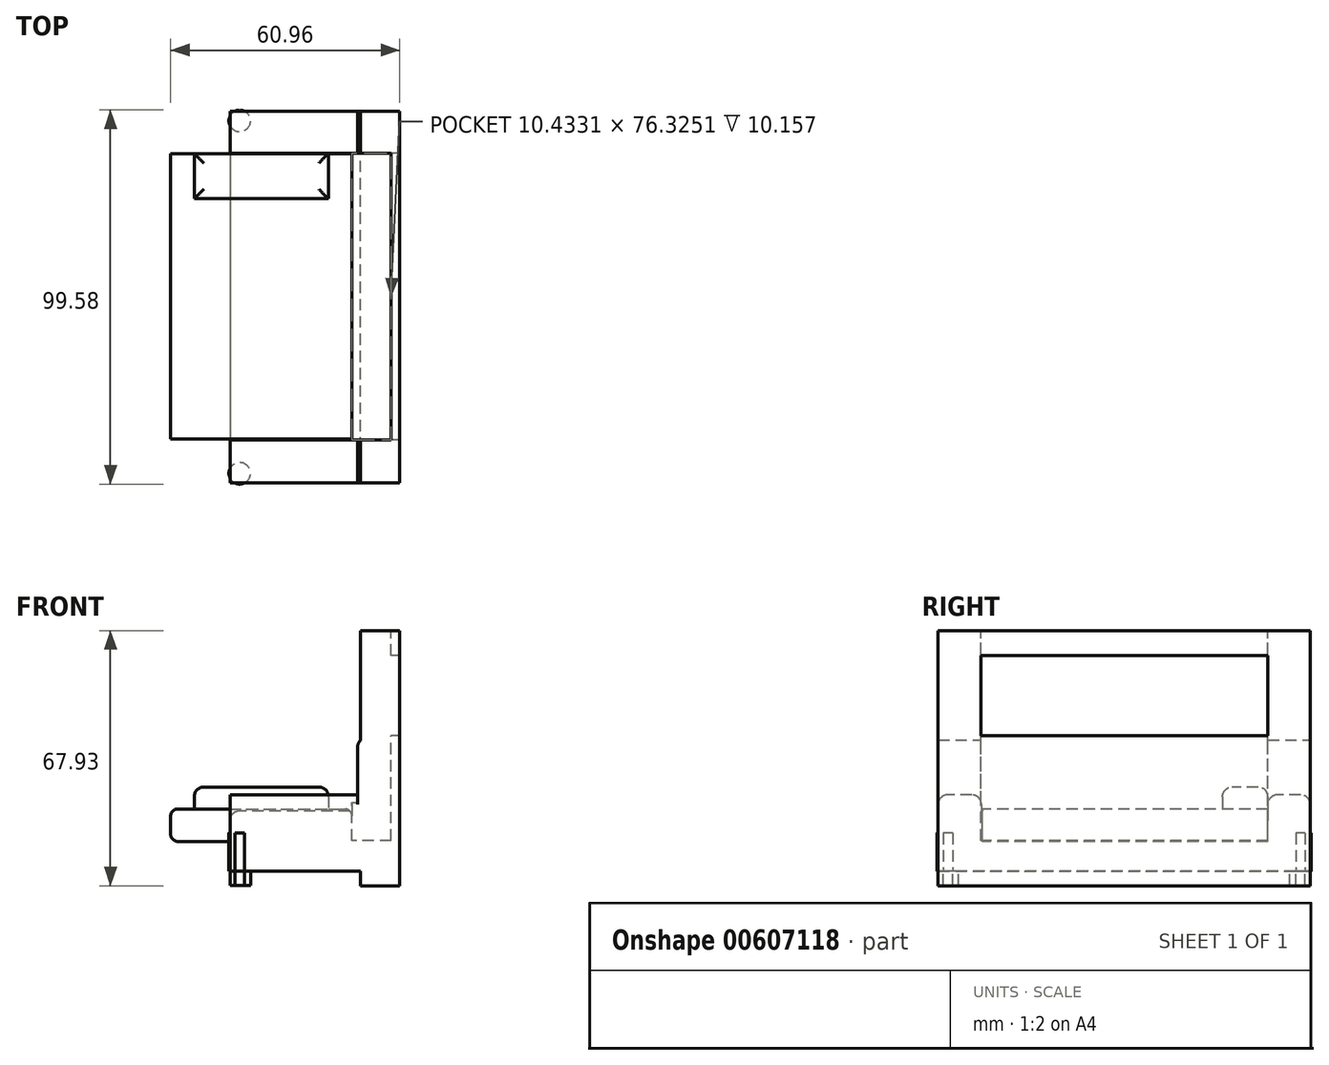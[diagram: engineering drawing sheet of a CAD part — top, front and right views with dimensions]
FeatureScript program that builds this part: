
annotation { "Feature Type Name" : "Feature", "Feature Type Description" : "" }
export const myFeature = defineFeature(function(context is Context, id is Id, definition is map)
    precondition{}
    {
        {
            var Q0;
            Q0=qCreatedBy(makeId("Top.planeOp"),FACE);
            var sketch = newSketch(context, id + "F0", { "sketchPlane" : qUnion([Q0])});
            skLineSegment(sketch, "E0.bottom", {"start": v(-36.7, 51.66) * mm, "end": v(8.5, 51.66) * mm});
            skLineSegment(sketch, "E0.top", {"start": v(-36.7, -47.34) * mm, "end": v(8.5, -47.34) * mm});
            skLineSegment(sketch, "E0.left", {"start": v(-36.7, 51.66) * mm, "end": v(-36.7, -47.34) * mm});
            skLineSegment(sketch, "E0.right", {"start": v(8.5, 51.66) * mm, "end": v(8.5, -47.34) * mm});
            skCircle(sketch, "E1", {"center": v(-34.1, 49.07) * mm, "radius": 2.88 * mm});
            skLineSegment(sketch, "E2", {"start": v(-14.1, 58) * mm, "end": v(-14.1, -55.7) * mm});
            skPoint(sketch, "E2.startSnap0", {"position": v(-14.1, 51.66) * mm});
            skLineSegment(sketch, "E3", {"start": v(-36.7, 2.16) * mm, "end": v(19.43, 2.16) * mm});
            skCircle(sketch, "E4.MirrorC", {"center": v(-34.1, -44.75) * mm, "radius": 2.88 * mm});
            skSolve(sketch);
        }
        {
            var Q0;
            Q0=qSketchRegion(id+"F0",true);
            extrude(context, id + "F1", {"entities" : qUnion([Q0]), "depth" : 10.16 * mm, "offsetDistance" : 25.4 * mm});
        }
        {
            var Q0;
            {var subQ0=sQuery(id+"F0.wireOp",EDGE,"51a0da69-c7e2-46c1-813b-57cbcf78bc440.MirrorC");var subQ1=sQuery(id+"F0.wireOp",EDGE,"E0.bottom");var subQ2=makeQuery(id+"F0.imprint","INTERSECT",VERTEX,{"disambiguationData":[OD(0.0)],"derivedFrom":[subQ1,subQ0]});Q0=makeQuery(id+"F0.imprint","IMPRINT",FACE,{"disambiguationData":[TD([[makeQuery(id+"F0.imprint","IMPRINT",EDGE,{"disambiguationData":[TD([[subQ2,-1.0]])],"derivedFrom":subQ1}),-1.0]])]});}
            var Q1;
            {var subQ0=sQuery(id+"F0.wireOp",EDGE,"E1");var subQ1=sQuery(id+"F0.wireOp",EDGE,"E0.bottom");var subQ2=makeQuery(id+"F0.imprint","INTERSECT",VERTEX,{"disambiguationData":[OD(0.0)],"derivedFrom":[subQ1,subQ0]});Q1=makeQuery(id+"F0.imprint","IMPRINT",FACE,{"disambiguationData":[TD([[makeQuery(id+"F0.imprint","IMPRINT",EDGE,{"disambiguationData":[TD([[subQ2,-1.0]])],"derivedFrom":subQ1}),-1.0]])]});}
            var Q2;
            {var subQ0=sQuery(id+"F0.wireOp",EDGE,"3a2c508c-d446-42d2-86cc-67812b7293b00.MirrorC");var subQ1=sQuery(id+"F0.wireOp",EDGE,"E0.top");var subQ2=makeQuery(id+"F0.imprint","INTERSECT",VERTEX,{"disambiguationData":[OD(0.0)],"derivedFrom":[subQ1,subQ0]});Q2=makeQuery(id+"F0.imprint","IMPRINT",FACE,{"disambiguationData":[TD([[makeQuery(id+"F0.imprint","IMPRINT",EDGE,{"disambiguationData":[TD([[subQ2,-1.0]])],"derivedFrom":subQ1}),1.0]])]});}
            var Q3;
            {var subQ0=sQuery(id+"F0.wireOp",EDGE,"E4.MirrorC");var subQ1=sQuery(id+"F0.wireOp",EDGE,"E0.top");var subQ2=makeQuery(id+"F0.imprint","INTERSECT",VERTEX,{"disambiguationData":[OD(0.0)],"derivedFrom":[subQ1,subQ0]});Q3=makeQuery(id+"F0.imprint","IMPRINT",FACE,{"disambiguationData":[TD([[makeQuery(id+"F0.imprint","IMPRINT",EDGE,{"disambiguationData":[TD([[subQ2,-1.0]])],"derivedFrom":subQ1}),1.0]])]});}
            extrude(context, id + "F2", {"entities" : qUnion([Q0, Q1, Q2, Q3]), "operationType" : NewBodyOperationType.ADD, "oppositeDirection" : true, "depth" : 3.8 * mm, "offsetDistance" : 25.4 * mm});
        }
        {
            var Q0;
            Q0=makeQuery(id+"F1.opExtrude","CAP_FACE",FACE,{"disambiguationData":[OSD([sQuery(id+"F0.wireOp",EDGE,"E0.bottom"),sQuery(id+"F0.wireOp",EDGE,"E0.top"),sQuery(id+"F0.wireOp",EDGE,"E0.left"),sQuery(id+"F0.wireOp",EDGE,"E0.right"),sQuery(id+"F0.wireOp",EDGE,"E1"),sQuery(id+"F0.wireOp",EDGE,"51a0da69-c7e2-46c1-813b-57cbcf78bc440.MirrorC"),sQuery(id+"F0.wireOp",EDGE,"E4.MirrorC"),sQuery(id+"F0.wireOp",EDGE,"3a2c508c-d446-42d2-86cc-67812b7293b00.MirrorC")])],"isStart":false});
            var sketch = newSketch(context, id + "F3", { "sketchPlane" : qUnion([Q0])});
            skLineSegment(sketch, "E5.bottom", {"start": v(8.5, 51.66) * mm, "end": v(-2.73, 51.66) * mm});
            skLineSegment(sketch, "E5.top", {"start": v(8.5, -47.34) * mm, "end": v(-2.73, -47.34) * mm});
            skLineSegment(sketch, "E5.left", {"start": v(8.5, 51.66) * mm, "end": v(8.5, -47.34) * mm});
            skLineSegment(sketch, "E5.right", {"start": v(-2.73, 51.66) * mm, "end": v(-2.73, -47.34) * mm});
            skSolve(sketch);
        }
        {
            var Q0;
            Q0=qSketchRegion(id+"F3",true);
            extrude(context, id + "F4", {"entities" : qUnion([Q0]), "operationType" : NewBodyOperationType.ADD, "depth" : 25.4 * mm, "offsetDistance" : 25.4 * mm});
        }
        {
            var Q0;
            {var subQ0=sQuery(id+"F0.wireOp",EDGE,"E0.left");var subQ1=sQuery(id+"F0.wireOp",EDGE,"E0.top");var subQ3=sQuery(id+"F0.wireOp",EDGE,"E4.MirrorC");var subQ7=sQuery(id+"F0.wireOp",EDGE,"E1");var subQ9=sQuery(id+"F0.wireOp",EDGE,"E0.bottom");var subQ12=sQuery(id+"F0.wireOp",EDGE,"E0.right");var subQ13=sQuery(id+"F0.wireOp",EDGE,"3a2c508c-d446-42d2-86cc-67812b7293b00.MirrorC");var subQ21=sQuery(id+"F0.wireOp",EDGE,"51a0da69-c7e2-46c1-813b-57cbcf78bc440.MirrorC");Q0=makeQuery(id+"F4.boolean.opBoolean","SPLIT",FACE,{"disambiguationData":[TD([makeQuery(id+"F4.opExtrude","SWEPT_FACE",FACE,{"disambiguationData":[OSD([sQuery(id+"F3.wireOp",EDGE,"E5.right")])]})])],"derivedFrom":makeQuery(id+"F1.opExtrude","CAP_FACE",FACE,{"disambiguationData":[OSD([subQ9,subQ1,subQ0,subQ12,subQ7,subQ21,subQ3,subQ13])],"isStart":false})});}
            var sketch = newSketch(context, id + "F5", { "sketchPlane" : qUnion([Q0])});
            skLineSegment(sketch, "E6.bottom", {"start": v(-2.73, 51.66) * mm, "end": v(-36.7, 51.66) * mm});
            skLineSegment(sketch, "E6.top", {"start": v(-2.73, 40.44) * mm, "end": v(-36.7, 40.44) * mm});
            skLineSegment(sketch, "E6.left", {"start": v(-2.73, 51.66) * mm, "end": v(-2.73, 40.44) * mm});
            skLineSegment(sketch, "E6.right", {"start": v(-36.7, 51.66) * mm, "end": v(-36.7, 40.44) * mm});
            skLineSegment(sketch, "E7.bottom", {"start": v(-2.73, -47.34) * mm, "end": v(-36.7, -47.34) * mm});
            skLineSegment(sketch, "E7.top", {"start": v(-2.73, -35.83) * mm, "end": v(-36.7, -35.83) * mm});
            skLineSegment(sketch, "E7.left", {"start": v(-2.73, -47.34) * mm, "end": v(-2.73, -35.83) * mm});
            skLineSegment(sketch, "E7.right", {"start": v(-36.7, -47.34) * mm, "end": v(-36.7, -35.83) * mm});
            skSolve(sketch);
        }
        {
            var Q0;
            {var subQ0=sQuery(id+"F5.wireOp",EDGE,"E6.top");Q0=makeQuery(id+"F5.imprint","IMPRINT",FACE,{"disambiguationData":[TD([[makeQuery(id+"F5.imprint","IMPRINT",EDGE,{"derivedFrom":subQ0}),-1.0]])]});}
            var Q1;
            {var subQ0=sQuery(id+"F5.wireOp",EDGE,"E7.top");Q1=makeQuery(id+"F5.imprint","IMPRINT",FACE,{"disambiguationData":[TD([[makeQuery(id+"F5.imprint","IMPRINT",EDGE,{"derivedFrom":subQ0}),1.0]])]});}
            extrude(context, id + "F6", {"entities" : qUnion([Q0, Q1]), "operationType" : NewBodyOperationType.ADD, "depth" : 10.16 * mm, "offsetDistance" : 25.4 * mm});
        }
        {
            var Q0;
            Q0=makeQuery(id+"F4.opExtrude","CAP_EDGE",EDGE,{"disambiguationData":[OSD([sQuery(id+"F3.wireOp",EDGE,"E5.right")])],"isStart":false});
            var Q1;
            Q1=makeQuery(id+"F6.opExtrude","CAP_EDGE",EDGE,{"disambiguationData":[OSD([sQuery(id+"F5.wireOp",EDGE,"E7.top")])],"isStart":false});
            var Q2;
            Q2=makeQuery(id+"F6.opExtrude","CAP_EDGE",EDGE,{"disambiguationData":[OSD([sQuery(id+"F5.wireOp",EDGE,"E7.bottom")])],"isStart":false});
            var Q3;
            Q3=makeQuery(id+"F6.opExtrude","CAP_EDGE",EDGE,{"disambiguationData":[OSD([sQuery(id+"F5.wireOp",EDGE,"E6.bottom")])],"isStart":false});
            var Q4;
            Q4=makeQuery(id+"F6.opExtrude","CAP_EDGE",EDGE,{"disambiguationData":[OSD([sQuery(id+"F5.wireOp",EDGE,"E6.top")])],"isStart":false});
            var Q5;
            Q5=makeQuery(id+"F4.opExtrude","CAP_EDGE",EDGE,{"disambiguationData":[OSD([sQuery(id+"F3.wireOp",EDGE,"E5.left")])],"isStart":false});
            fillet(context, id + "F7", {"entities" : qUnion([Q0, Q1, Q2, Q3, Q4, Q5]), "radius" : 2.54 * mm, "tangentPropagation" : true, "allowEdgeOverflow" : false});
        }
        {
            var Q0;
            {var subQ0=makeQuery(id+"F4.opExtrude","SWEPT_FACE",FACE,{"disambiguationData":[OSD([sQuery(id+"F3.wireOp",EDGE,"E5.right")])]});var subQ1=sQuery(id+"F0.wireOp",EDGE,"E0.left");var subQ2=sQuery(id+"F0.wireOp",EDGE,"E0.top");var subQ4=sQuery(id+"F0.wireOp",EDGE,"E4.MirrorC");var subQ9=sQuery(id+"F0.wireOp",EDGE,"E1");var subQ12=sQuery(id+"F0.wireOp",EDGE,"E0.bottom");var subQ16=sQuery(id+"F0.wireOp",EDGE,"E0.right");var subQ17=sQuery(id+"F0.wireOp",EDGE,"3a2c508c-d446-42d2-86cc-67812b7293b00.MirrorC");var subQ25=sQuery(id+"F0.wireOp",EDGE,"51a0da69-c7e2-46c1-813b-57cbcf78bc440.MirrorC");Q0=makeQuery(id+"F6.boolean.opBoolean","SPLIT",FACE,{"disambiguationData":[TD([subQ0])],"derivedFrom":makeQuery(id+"F4.boolean.opBoolean","SPLIT",FACE,{"disambiguationData":[TD([subQ0])],"derivedFrom":makeQuery(id+"F1.opExtrude","CAP_FACE",FACE,{"disambiguationData":[OSD([subQ12,subQ2,subQ1,subQ16,subQ9,subQ25,subQ4,subQ17])],"isStart":false})})});}
            var sketch = newSketch(context, id + "F8", { "sketchPlane" : qUnion([Q0])});
            skLineSegment(sketch, "E8.bottom", {"start": v(-2.73, 40.44) * mm, "end": v(-36.7, 40.44) * mm});
            skLineSegment(sketch, "E8.top", {"start": v(-2.73, 2.3) * mm, "end": v(-36.7, 2.3) * mm});
            skLineSegment(sketch, "E8.left", {"start": v(-2.73, 40.44) * mm, "end": v(-2.73, 2.3) * mm});
            skLineSegment(sketch, "E8.right", {"start": v(-36.7, 40.44) * mm, "end": v(-36.7, 2.3) * mm});
            skLineSegment(sketch, "E9.bottom", {"start": v(-2.73, -35.83) * mm, "end": v(-36.7, -35.83) * mm});
            skLineSegment(sketch, "E9.top", {"start": v(-2.73, 1.3) * mm, "end": v(-36.7, 1.3) * mm});
            skLineSegment(sketch, "E9.left", {"start": v(-2.73, -35.83) * mm, "end": v(-2.73, 1.3) * mm});
            skLineSegment(sketch, "E9.right", {"start": v(-36.7, -35.83) * mm, "end": v(-36.7, 1.3) * mm});
            skSolve(sketch);
        }
        {
            var Q0;
            Q0=makeQuery(id+"F8.imprint","IMPRINT",FACE,{"disambiguationData":[TD([[makeQuery(id+"F8.imprint","IMPRINT",EDGE,{"derivedFrom":sQuery(id+"F8.wireOp",EDGE,"E8.bottom")}),1.0]])]});
            var Q1;
            Q1=makeQuery(id+"F8.imprint","IMPRINT",FACE,{"disambiguationData":[TD([[makeQuery(id+"F8.imprint","IMPRINT",EDGE,{"derivedFrom":sQuery(id+"F8.wireOp",EDGE,"E9.bottom")}),-1.0]])]});
            extrude(context, id + "F9", {"entities" : qUnion([Q0, Q1]), "operationType" : NewBodyOperationType.ADD, "depth" : 5.84 * mm, "offsetDistance" : 25.4 * mm});
        }
        {
            var Q0;
            Q0=makeQuery(id+"F9.opExtrude","CAP_EDGE",EDGE,{"disambiguationData":[OSD([sQuery(id+"F8.wireOp",EDGE,"E9.top")])],"isStart":false});
            var Q1;
            Q1=makeQuery(id+"F9.opExtrude","CAP_EDGE",EDGE,{"disambiguationData":[OSD([sQuery(id+"F8.wireOp",EDGE,"E8.top")])],"isStart":false});
            var Q2;
            Q2=makeQuery(id+"F9.opExtrude","CAP_EDGE",EDGE,{"disambiguationData":[OSD([sQuery(id+"F8.wireOp",EDGE,"E9.right")])],"isStart":false});
            var Q3;
            Q3=makeQuery(id+"F9.opExtrude","CAP_EDGE",EDGE,{"disambiguationData":[OSD([sQuery(id+"F8.wireOp",EDGE,"E8.right")])],"isStart":false});
            fillet(context, id + "F10", {"entities" : qUnion([Q0, Q1, Q2, Q3]), "radius" : 2.54 * mm, "tangentPropagation" : true, "allowEdgeOverflow" : false});
        }
        {
            var Q0;
            {var subQ0=sQuery(id+"F0.wireOp",EDGE,"E0.right");var subQ2=makeQuery(id+"F0.imprint","INTERSECT",VERTEX,{"derivedFrom":[subQ0,sQuery(id+"F0.wireOp",EDGE,"E3")]});Q0=makeQuery(id+"F4.boolean.opBoolean","MERGE",FACE,{"derivedFrom":[makeQuery(id+"F1.opExtrude","SWEPT_FACE",FACE,{"disambiguationData":[OSD([subQ0]),TDD([makeQuery(id+"F0.imprint","IMPRINT",EDGE,{"disambiguationData":[TD([[makeQuery(id+"F0.imprint","INTERSECT",VERTEX,{"derivedFrom":[sQuery(id+"F0.wireOp",EDGE,"E0.bottom"),subQ0]}),-1.0]])],"derivedFrom":subQ0})])]}),makeQuery(id+"F1.opExtrude","SWEPT_FACE",FACE,{"disambiguationData":[OSD([subQ0]),TDD([makeQuery(id+"F0.imprint","IMPRINT",EDGE,{"disambiguationData":[TD([[subQ2,1.0]])],"derivedFrom":subQ0}),makeQuery(id+"F0.imprint","IMPRINT",EDGE,{"disambiguationData":[TD([[subQ2,-1.0]])],"derivedFrom":subQ0})])]}),makeQuery(id+"F1.opExtrude","SWEPT_FACE",FACE,{"disambiguationData":[OSD([subQ0]),TDD([makeQuery(id+"F0.imprint","IMPRINT",EDGE,{"disambiguationData":[TD([[makeQuery(id+"F0.imprint","INTERSECT",VERTEX,{"derivedFrom":[sQuery(id+"F0.wireOp",EDGE,"E0.top"),subQ0]}),1.0]])],"derivedFrom":subQ0})])]}),makeQuery(id+"F4.opExtrude","SWEPT_FACE",FACE,{"disambiguationData":[OSD([sQuery(id+"F3.wireOp",EDGE,"E5.left")])]})]});}
            var sketch = newSketch(context, id + "F11", { "sketchPlane" : qUnion([Q0])});
            skLineSegment(sketch, "E10.bottom", {"start": v(-47.34, 64.04) * mm, "end": v(51.66, 64.04) * mm});
            skLineSegment(sketch, "E10.top", {"start": v(-47.34, -3.89) * mm, "end": v(51.66, -3.89) * mm});
            skLineSegment(sketch, "E10.left", {"start": v(-47.34, 64.04) * mm, "end": v(-47.34, -3.89) * mm});
            skLineSegment(sketch, "E10.right", {"start": v(51.66, 64.04) * mm, "end": v(51.66, -3.89) * mm});
            skLineSegment(sketch, "E11.bottom", {"start": v(40.38, 7.91) * mm, "end": v(-35.6, 7.91) * mm});
            skLineSegment(sketch, "E11.top", {"start": v(40.38, 16.55) * mm, "end": v(-35.6, 16.55) * mm});
            skLineSegment(sketch, "E11.left", {"start": v(40.38, 7.91) * mm, "end": v(40.38, 16.55) * mm});
            skLineSegment(sketch, "E11.right", {"start": v(-35.6, 7.91) * mm, "end": v(-35.6, 16.55) * mm});
            skSolve(sketch);
        }
        {
            var Q0;
            Q0=qSketchRegion(id+"F11",true);
            extrude(context, id + "F12", {"entities" : qUnion([Q0]), "operationType" : NewBodyOperationType.ADD, "oppositeDirection" : true, "depth" : 10.4 * mm, "offsetDistance" : 25.4 * mm});
        }
        {
            var Q0;
            {var subQ0=sQuery(id+"F11.wireOp",EDGE,"E10.bottom");var subQ10=sQuery(id+"F11.wireOp",EDGE,"E10.left");var subQ11=sQuery(id+"F11.wireOp",EDGE,"E10.right");Q0=makeQuery(id+"F12.boolean.opBoolean","SPLIT",FACE,{"disambiguationData":[TD([makeQuery(id+"F7.opFillet","BLEND_FACE",FACE,{"disambiguationData":[OSD([sQuery(id+"F3.wireOp",EDGE,"E5.right")])]})])],"derivedFrom":makeQuery(id+"F12.opExtrude","CAP_FACE",FACE,{"disambiguationData":[OSD([subQ0,sQuery(id+"F11.wireOp",EDGE,"E10.top"),subQ10,subQ11])],"isStart":false})});}
            var sketch = newSketch(context, id + "F13", { "sketchPlane" : qUnion([Q0])});
            skLineSegment(sketch, "E12.bottom", {"start": v(35.83, 34.88) * mm, "end": v(-40.44, 34.88) * mm});
            skLineSegment(sketch, "E12.top", {"start": v(35.83, 64.04) * mm, "end": v(-40.44, 64.04) * mm});
            skLineSegment(sketch, "E12.left", {"start": v(35.83, 34.88) * mm, "end": v(35.83, 64.04) * mm});
            skLineSegment(sketch, "E12.right", {"start": v(-40.44, 34.88) * mm, "end": v(-40.44, 64.04) * mm});
            skLineSegment(sketch, "E13.bottom", {"start": v(-40.44, 64.04) * mm, "end": v(-40.44, 64.04) * mm});
            skLineSegment(sketch, "E13.top", {"start": v(-40.44, 34.88) * mm, "end": v(-40.44, 34.88) * mm});
            skLineSegment(sketch, "E13.left", {"start": v(-40.44, 64.04) * mm, "end": v(-40.44, 34.88) * mm});
            skLineSegment(sketch, "E13.right", {"start": v(-40.44, 64.04) * mm, "end": v(-40.44, 34.88) * mm});
            skLineSegment(sketch, "E14", {"start": v(-2.16, 64.04) * mm, "end": v(-2.16, 34.88) * mm});
            skLineSegment(sketch, "E15", {"start": v(-2.16, 64.04) * mm, "end": v(35.83, 64.04) * mm});
            skLineSegment(sketch, "E16", {"start": v(16.84, 64.04) * mm, "end": v(16.84, 34.88) * mm});
            skLineSegment(sketch, "E17", {"start": v(16.84, 34.88) * mm, "end": v(-40.44, 34.88) * mm});
            skLineSegment(sketch, "E18", {"start": v(-40.44, 64.04) * mm, "end": v(-2.16, 64.04) * mm});
            skLineSegment(sketch, "E19", {"start": v(-21.3, 64.04) * mm, "end": v(-21.3, 34.88) * mm});
            skLineSegment(sketch, "E20", {"start": v(-20.43, 64.04) * mm, "end": v(-20.43, 34.88) * mm});
            skLineSegment(sketch, "E21", {"start": v(-1.4, 64.04) * mm, "end": v(-1.4, 34.88) * mm});
            skLineSegment(sketch, "E22", {"start": v(17.73, 64.04) * mm, "end": v(17.73, 34.88) * mm});
            skLineSegment(sketch, "E23", {"start": v(36.84, 64.04) * mm, "end": v(36.84, 34.88) * mm});
            skLineSegment(sketch, "E24.bottom", {"start": v(-33.58, 61.49) * mm, "end": v(-27.07, 61.49) * mm});
            skLineSegment(sketch, "E24.top", {"start": v(-33.58, 60.67) * mm, "end": v(-27.07, 60.67) * mm});
            skLineSegment(sketch, "E24.left", {"start": v(-33.58, 61.49) * mm, "end": v(-33.58, 60.67) * mm});
            skLineSegment(sketch, "E24.right", {"start": v(-27.07, 61.49) * mm, "end": v(-27.07, 60.67) * mm});
            skLineSegment(sketch, "E25.bottom", {"start": v(-15.26, 61.49) * mm, "end": v(-7.73, 61.49) * mm});
            skLineSegment(sketch, "E25.top", {"start": v(-15.26, 60.67) * mm, "end": v(-7.73, 60.67) * mm});
            skLineSegment(sketch, "E25.left", {"start": v(-15.26, 61.49) * mm, "end": v(-15.26, 60.67) * mm});
            skLineSegment(sketch, "E25.right", {"start": v(-7.73, 61.49) * mm, "end": v(-7.73, 60.67) * mm});
            skLineSegment(sketch, "E26.bottom", {"start": v(4.38, 60.67) * mm, "end": v(11.5, 60.67) * mm});
            skLineSegment(sketch, "E26.top", {"start": v(4.38, 61.49) * mm, "end": v(11.5, 61.49) * mm});
            skLineSegment(sketch, "E26.left", {"start": v(4.38, 60.67) * mm, "end": v(4.38, 61.49) * mm});
            skLineSegment(sketch, "E26.right", {"start": v(11.5, 60.67) * mm, "end": v(11.5, 61.49) * mm});
            skLineSegment(sketch, "E27.bottom", {"start": v(23.5, 61.49) * mm, "end": v(30.63, 61.49) * mm});
            skLineSegment(sketch, "E27.top", {"start": v(23.5, 60.67) * mm, "end": v(30.63, 60.67) * mm});
            skLineSegment(sketch, "E27.left", {"start": v(23.5, 61.49) * mm, "end": v(23.5, 60.67) * mm});
            skLineSegment(sketch, "E27.right", {"start": v(30.63, 61.49) * mm, "end": v(30.63, 60.67) * mm});
            skSolve(sketch);
        }
        {
            var Q0;
            {var subQ0=sQuery(id+"F13.wireOp",EDGE,"E13.right");Q0=makeQuery(id+"F13.imprint","IMPRINT",FACE,{"disambiguationData":[TD([[makeQuery(id+"F13.imprint","IMPRINT",EDGE,{"derivedFrom":subQ0}),1.0]])]});}
            var Q1;
            {var subQ0=sQuery(id+"F13.wireOp",EDGE,"E14");Q1=makeQuery(id+"F13.imprint","IMPRINT",FACE,{"disambiguationData":[TD([[makeQuery(id+"F13.imprint","IMPRINT",EDGE,{"derivedFrom":subQ0}),-1.0]])]});}
            var Q2;
            {var subQ0=sQuery(id+"F13.wireOp",EDGE,"E16");Q2=makeQuery(id+"F13.imprint","IMPRINT",FACE,{"disambiguationData":[TD([[makeQuery(id+"F13.imprint","IMPRINT",EDGE,{"derivedFrom":subQ0}),-1.0]])]});}
            var Q3;
            {var subQ0=sQuery(id+"F13.wireOp",EDGE,"E12.left");Q3=makeQuery(id+"F13.imprint","IMPRINT",FACE,{"disambiguationData":[TD([[makeQuery(id+"F13.imprint","IMPRINT",EDGE,{"derivedFrom":subQ0}),1.0]])]});}
            extrude(context, id + "F14", {"entities" : qUnion([Q0, Q1, Q2, Q3]), "operationType" : NewBodyOperationType.ADD, "depth" : 0.25 * mm, "offsetDistance" : 25.4 * mm});
        }
        {
            var Q0;
            Q0=makeQuery(id+"F13.imprint","IMPRINT",FACE,{"disambiguationData":[TD([[makeQuery(id+"F13.imprint","IMPRINT",EDGE,{"derivedFrom":sQuery(id+"F13.wireOp",EDGE,"E27.bottom")}),-1.0]])]});
            var Q1;
            Q1=makeQuery(id+"F13.imprint","IMPRINT",FACE,{"disambiguationData":[TD([[makeQuery(id+"F13.imprint","IMPRINT",EDGE,{"derivedFrom":sQuery(id+"F13.wireOp",EDGE,"E26.bottom")}),1.0]])]});
            var Q2;
            Q2=makeQuery(id+"F13.imprint","IMPRINT",FACE,{"disambiguationData":[TD([[makeQuery(id+"F13.imprint","IMPRINT",EDGE,{"derivedFrom":sQuery(id+"F13.wireOp",EDGE,"E25.bottom")}),-1.0]])]});
            var Q3;
            Q3=makeQuery(id+"F13.imprint","IMPRINT",FACE,{"disambiguationData":[TD([[makeQuery(id+"F13.imprint","IMPRINT",EDGE,{"derivedFrom":sQuery(id+"F13.wireOp",EDGE,"E24.bottom")}),-1.0]])]});
            extrude(context, id + "F15", {"entities" : qUnion([Q0, Q1, Q2, Q3]), "operationType" : NewBodyOperationType.ADD, "depth" : 1.52 * mm, "offsetDistance" : 25.4 * mm});
        }
        {
            var Q0;
            Q0=makeQuery(id+"F11.imprint","IMPRINT",FACE,{"disambiguationData":[TD([[makeQuery(id+"F11.imprint","IMPRINT",EDGE,{"derivedFrom":sQuery(id+"F11.wireOp",EDGE,"E11.bottom")}),-1.0]])]});
            extrude(context, id + "F16", {"entities" : qUnion([Q0]), "operationType" : NewBodyOperationType.ADD, "oppositeDirection" : true, "depth" : 60.96 * mm, "offsetDistance" : 25.4 * mm});
        }
        {
            var Q0;
            {var subQ0=sQuery(id+"F13.wireOp",EDGE,"E18");var subQ1=sQuery(id+"F11.wireOp",EDGE,"E10.bottom");var subQ3=sQuery(id+"F13.wireOp",EDGE,"E15");Q0=makeQuery(id+"F14.boolean.opBoolean","MERGE",FACE,{"derivedFrom":[makeQuery(id+"F12.opExtrude","SWEPT_FACE",FACE,{"disambiguationData":[OSD([subQ1])]}),makeQuery(id+"F14.opExtrude","SWEPT_FACE",FACE,{"disambiguationData":[OSD([subQ3]),TDD([makeQuery(id+"F13.imprint","IMPRINT",EDGE,{"disambiguationData":[TD([[makeQuery(id+"F13.imprint","INTERSECT",VERTEX,{"derivedFrom":[subQ3,sQuery(id+"F13.wireOp",EDGE,"E22")]}),1.0]])],"derivedFrom":subQ3})])]}),makeQuery(id+"F14.opExtrude","SWEPT_FACE",FACE,{"disambiguationData":[OSD([subQ3]),TDD([makeQuery(id+"F13.imprint","IMPRINT",EDGE,{"disambiguationData":[TD([[makeQuery(id+"F13.imprint","INTERSECT",VERTEX,{"derivedFrom":[subQ3,sQuery(id+"F13.wireOp",EDGE,"E16")]}),-1.0]])],"derivedFrom":subQ3})])]}),makeQuery(id+"F14.opExtrude","SWEPT_FACE",FACE,{"disambiguationData":[OSD([subQ0]),TDD([makeQuery(id+"F13.imprint","IMPRINT",EDGE,{"disambiguationData":[TD([[makeQuery(id+"F13.imprint","INTERSECT",VERTEX,{"derivedFrom":[subQ0,sQuery(id+"F13.wireOp",EDGE,"E20")]}),1.0]])],"derivedFrom":subQ0})])]}),makeQuery(id+"F14.opExtrude","SWEPT_FACE",FACE,{"disambiguationData":[OSD([subQ0]),TDD([makeQuery(id+"F13.imprint","IMPRINT",EDGE,{"disambiguationData":[TD([[makeQuery(id+"F13.imprint","INTERSECT",VERTEX,{"derivedFrom":[subQ0,sQuery(id+"F13.wireOp",EDGE,"E19")]}),-1.0]])],"derivedFrom":subQ0})])]})]});}
            var sketch = newSketch(context, id + "F17", { "sketchPlane" : qUnion([Q0])});
            skLineSegment(sketch, "E28.bottom", {"start": v(-1.92, 40.44) * mm, "end": v(6.19, 40.44) * mm});
            skLineSegment(sketch, "E28.top", {"start": v(-1.92, -35.89) * mm, "end": v(6.19, -35.89) * mm});
            skLineSegment(sketch, "E28.left", {"start": v(-1.92, 40.44) * mm, "end": v(-1.92, -35.89) * mm});
            skLineSegment(sketch, "E28.right", {"start": v(6.19, 40.44) * mm, "end": v(6.19, -35.89) * mm});
            skPoint(sketch, "E29.oppositeSnap0", {"position": v(2.13, -35.89) * mm});
            skLineSegment(sketch, "E29.bottom", {"start": v(6.19, 40.44) * mm, "end": v(-4.25, 40.44) * mm});
            skLineSegment(sketch, "E29.top", {"start": v(6.19, -35.89) * mm, "end": v(-4.25, -35.89) * mm});
            skLineSegment(sketch, "E29.right", {"start": v(-4.25, 40.44) * mm, "end": v(-4.25, -35.89) * mm});
            skSolve(sketch);
        }
        {
            var Q0;
            Q0 = qSketchRegion(id + "F17", true);
            extrude(context, id + "F18", {"entities" : qUnion([Q0]), "operationType" : NewBodyOperationType.REMOVE, "oppositeDirection" : true, "depth" : 55.88 * mm, "offsetDistance" : 25.4 * mm});
        }
        {
            var Q0;
            Q0=makeQuery(id+"F16.opExtrude","CAP_EDGE",EDGE,{"disambiguationData":[OSD([sQuery(id+"F11.wireOp",EDGE,"E11.top")])],"isStart":false});
            var Q1;
            Q1=makeQuery(id+"F16.opExtrude","CAP_EDGE",EDGE,{"disambiguationData":[OSD([sQuery(id+"F11.wireOp",EDGE,"E11.bottom")])],"isStart":false});
            fillet(context, id + "F19", {"entities" : qUnion([Q0, Q1]), "radius" : 1.84 * mm, "tangentPropagation" : true, "allowEdgeOverflow" : false});
        }
        {
            var Q0;
            Q0=makeQuery(id+"F18.boolean.opBoolean","INTERSECT",EDGE,{"derivedFrom":[makeQuery(id+"F16.opExtrude","SWEPT_FACE",FACE,{"disambiguationData":[OSD([sQuery(id+"F11.wireOp",EDGE,"E11.top")])]}),makeQuery(id+"F18.opExtrude","SWEPT_FACE",FACE,{"disambiguationData":[OSD([sQuery(id+"F17.wireOp",EDGE,"E29.right")])]})]});
            fillet(context, id + "F20", {"entities" : qUnion([Q0]), "radius" : 1.84 * mm, "tangentPropagation" : true, "allowEdgeOverflow" : false});
        }
        {
            var Q0;
            Q0=makeQuery(id+"F16.opExtrude","SWEPT_FACE",FACE,{"disambiguationData":[OSD([sQuery(id+"F11.wireOp",EDGE,"E11.top")])]});
            var sketch = newSketch(context, id + "F21", { "sketchPlane" : qUnion([Q0])});
            skLineSegment(sketch, "E30.bottom", {"start": v(-46.2, 40.38) * mm, "end": v(-10.5, 40.38) * mm});
            skLineSegment(sketch, "E30.top", {"start": v(-46.2, 28.35) * mm, "end": v(-10.5, 28.35) * mm});
            skLineSegment(sketch, "E30.left", {"start": v(-46.2, 40.38) * mm, "end": v(-46.2, 28.35) * mm});
            skLineSegment(sketch, "E30.right", {"start": v(-10.5, 40.38) * mm, "end": v(-10.5, 28.35) * mm});
            skSolve(sketch);
        }
        {
            var Q0;
            Q0 = qSketchRegion(id + "F21", true);
            extrude(context, id + "F22", {"entities" : qUnion([Q0]), "operationType" : NewBodyOperationType.ADD, "depth" : 5.84 * mm, "offsetDistance" : 25.4 * mm});
        }
        {
            var Q0;
            Q0=makeQuery(id+"F22.opExtrude","CAP_EDGE",EDGE,{"disambiguationData":[OSD([sQuery(id+"F21.wireOp",EDGE,"E30.right")])],"isStart":false});
            var Q1;
            Q1=makeQuery(id+"F22.opExtrude","CAP_EDGE",EDGE,{"disambiguationData":[OSD([sQuery(id+"F21.wireOp",EDGE,"E30.top")])],"isStart":false});
            var Q2;
            Q2=makeQuery(id+"F22.opExtrude","CAP_EDGE",EDGE,{"disambiguationData":[OSD([sQuery(id+"F21.wireOp",EDGE,"E30.left")])],"isStart":false});
            var Q3;
            Q3=makeQuery(id+"F22.opExtrude","CAP_EDGE",EDGE,{"disambiguationData":[OSD([sQuery(id+"F21.wireOp",EDGE,"E30.bottom")])],"isStart":false});
            fillet(context, id + "F23", {"entities" : qUnion([Q0, Q1, Q2, Q3]), "radius" : 2.54 * mm, "tangentPropagation" : true, "allowEdgeOverflow" : false});
        }
        {
            var Q0;
            Q0=makeQuery(id+"F18.boolean.opBoolean","COPY",FACE,{"derivedFrom":makeQuery(id+"F18.opExtrude","SWEPT_FACE",FACE,{"disambiguationData":[OSD([sQuery(id+"F17.wireOp",EDGE,"E28.right")])]})});
            var sketch = newSketch(context, id + "F24", { "sketchPlane" : qUnion([Q0])});
            skLineSegment(sketch, "E31.bottom", {"start": v(-40.44, 57.42) * mm, "end": v(35.89, 57.42) * mm});
            skLineSegment(sketch, "E31.top", {"start": v(-40.44, 36.1) * mm, "end": v(35.89, 36.1) * mm});
            skLineSegment(sketch, "E31.left", {"start": v(-40.44, 57.42) * mm, "end": v(-40.44, 36.1) * mm});
            skLineSegment(sketch, "E31.right", {"start": v(35.89, 57.42) * mm, "end": v(35.89, 36.1) * mm});
            skSolve(sketch);
        }
        {
            var Q0;
            Q0 = qSketchRegion(id + "F24", true);
            extrude(context, id + "F25", {"entities" : qUnion([Q0]), "operationType" : NewBodyOperationType.REMOVE, "oppositeDirection" : true, "depth" : 25.4 * mm, "offsetDistance" : 25.4 * mm});
        }
    });
